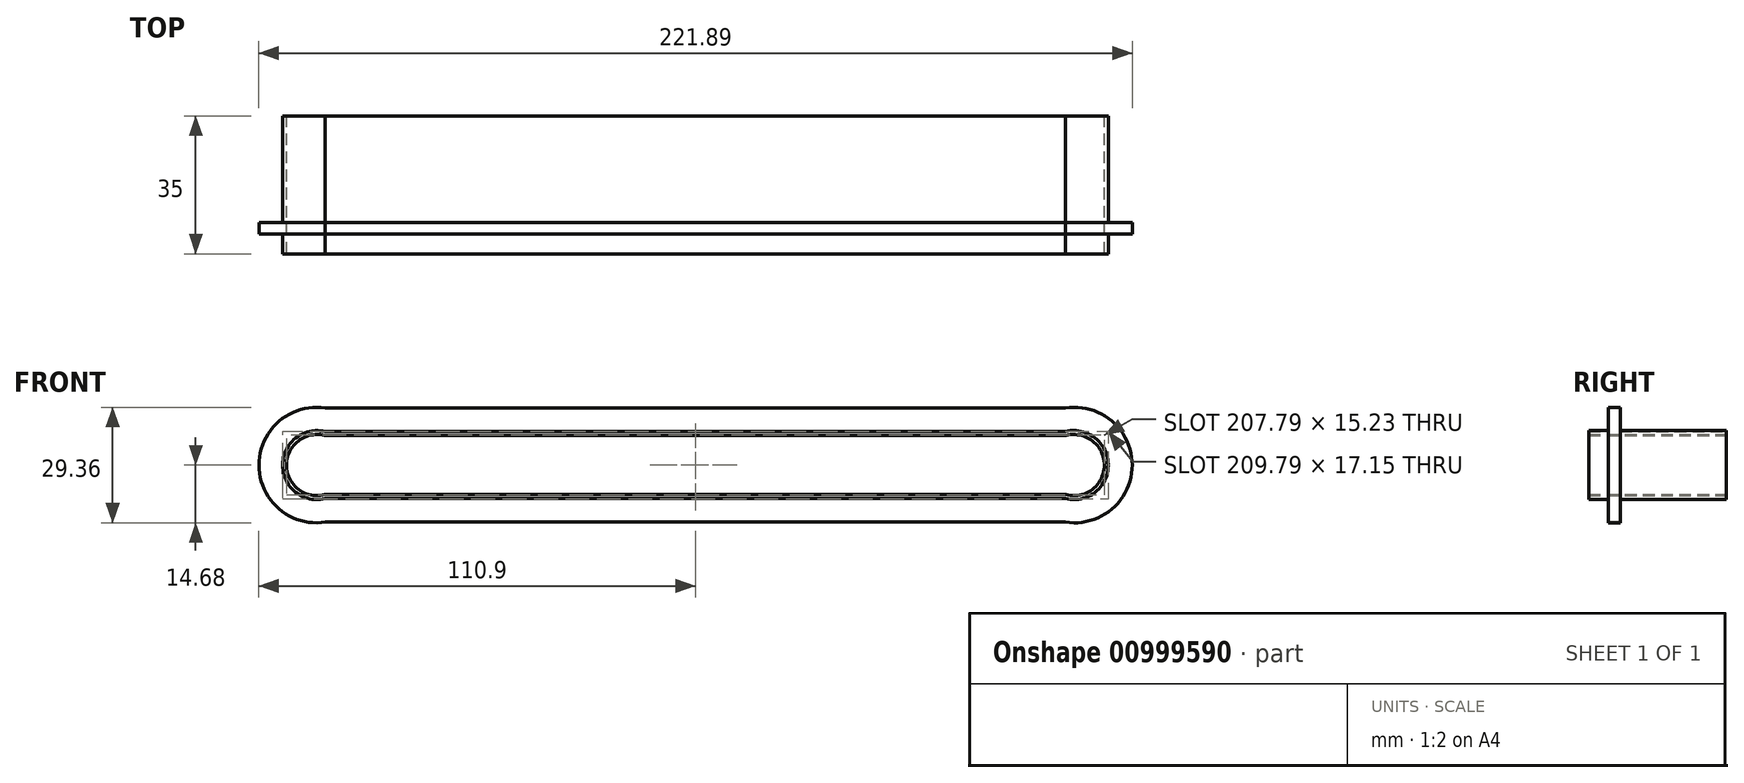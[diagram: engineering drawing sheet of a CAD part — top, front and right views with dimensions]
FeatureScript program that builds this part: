
annotation { "Feature Type Name" : "Feature", "Feature Type Description" : "" }
export const myFeature = defineFeature(function(context is Context, id is Id, definition is map)
    precondition{}
    {
        {
            var Q0;
            Q0=qCreatedBy(makeId("Front.planeOp"),FACE);
            var sketch = newSketch(context, id + "F0", { "sketchPlane" : qUnion([Q0])});
            skLineSegment(sketch, "E0.bottom", {"start": v(105, 8.5) * mm, "end": v(-105, 8.5) * mm});
            skLineSegment(sketch, "E0.top", {"start": v(105, -8.5) * mm, "end": v(-105, -8.5) * mm});
            skLineSegment(sketch, "E0.left", {"start": v(105, 8.5) * mm, "end": v(105, -8.5) * mm});
            skLineSegment(sketch, "E0.right", {"start": v(-105, 8.5) * mm, "end": v(-105, -8.5) * mm});
            skPoint(sketch, "E0.middle", {"position": v(0, 0) * mm});
            skLineSegment(sketch, "E1", {"start": v(0, -8.5) * mm, "end": v(94, -8.5) * mm});
            skLineSegment(sketch, "E2", {"start": v(94, -8.5) * mm, "end": v(-94, -8.5) * mm});
            skLineSegment(sketch, "E3", {"start": v(0, 8.5) * mm, "end": v(94, 8.5) * mm});
            skLineSegment(sketch, "E4", {"start": v(94, 8.5) * mm, "end": v(-94, 8.5) * mm});
            skArc(sketch, "E5", {"start": v(-94, 8.5) * mm, "mid": v(-104.89, 0) * mm, "end": v(-94, -8.5) * mm});
            skArc(sketch, "E6", {"start": v(94, -8.5) * mm, "mid": v(104.9, 0) * mm, "end": v(94, 8.5) * mm});
            skLineSegment(sketch, "E7", {"start": v(94, 8.5) * mm, "end": v(94, 14.5) * mm});
            skLineSegment(sketch, "E8", {"start": v(94, -8.5) * mm, "end": v(94, -14.5) * mm});
            skLineSegment(sketch, "E9", {"start": v(-94, 8.5) * mm, "end": v(-94, 14.5) * mm});
            skLineSegment(sketch, "E10", {"start": v(-94, -8.5) * mm, "end": v(-94, -14.5) * mm});
            skLineSegment(sketch, "E11", {"start": v(-94, -14.5) * mm, "end": v(94, -14.5) * mm});
            skLineSegment(sketch, "E12", {"start": v(94, 14.5) * mm, "end": v(-94, 14.5) * mm});
            skLineSegment(sketch, "E13", {"start": v(-104.89, 0) * mm, "end": v(-110.89, 0) * mm});
            skLineSegment(sketch, "E14", {"start": v(105, 0) * mm, "end": v(111, 0) * mm});
            skArc(sketch, "E15", {"start": v(-94, 14.5) * mm, "mid": v(-110.89, 0) * mm, "end": v(-94, -14.5) * mm});
            skArc(sketch, "E16", {"start": v(94, -14.5) * mm, "mid": v(111, 0) * mm, "end": v(94, 14.5) * mm});
            skSolve(sketch);
        }
        {
            var Q0;
            {var subQ0=sQuery(id+"F0.wireOp",EDGE,"E6");var subQ1=sQuery(id+"F0.wireOp",EDGE,"E0.bottom");var subQ3=makeQuery(id+"F0.imprint","INTERSECT",VERTEX,{"derivedFrom":[subQ1,subQ0]});Q0=makeQuery(id+"F0.imprint","IMPRINT",FACE,{"disambiguationData":[TD([[makeQuery(id+"F0.imprint","IMPRINT",EDGE,{"disambiguationData":[TD([[subQ3,-1.0]])],"derivedFrom":subQ1}),-1.0]])]});}
            var Q1;
            {var subQ0=sQuery(id+"F0.wireOp",EDGE,"E5");var subQ1=sQuery(id+"F0.wireOp",EDGE,"E0.bottom");var subQ2=makeQuery(id+"F0.imprint","INTERSECT",VERTEX,{"derivedFrom":[subQ1,subQ0]});Q1=makeQuery(id+"F0.imprint","IMPRINT",FACE,{"disambiguationData":[TD([[makeQuery(id+"F0.imprint","IMPRINT",EDGE,{"disambiguationData":[TD([[subQ2,1.0]])],"derivedFrom":subQ1}),-1.0]])]});}
            var Q2;
            {var subQ0=sQuery(id+"F0.wireOp",EDGE,"E6");var subQ1=sQuery(id+"F0.wireOp",EDGE,"E0.top");var subQ3=makeQuery(id+"F0.imprint","INTERSECT",VERTEX,{"derivedFrom":[subQ1,subQ0]});Q2=makeQuery(id+"F0.imprint","IMPRINT",FACE,{"disambiguationData":[TD([[makeQuery(id+"F0.imprint","IMPRINT",EDGE,{"disambiguationData":[TD([[subQ3,-1.0]])],"derivedFrom":subQ1}),1.0]])]});}
            var Q3;
            {var subQ0=sQuery(id+"F0.wireOp",EDGE,"E5");var subQ1=sQuery(id+"F0.wireOp",EDGE,"E0.top");var subQ2=makeQuery(id+"F0.imprint","INTERSECT",VERTEX,{"derivedFrom":[subQ1,subQ0]});Q3=makeQuery(id+"F0.imprint","IMPRINT",FACE,{"disambiguationData":[TD([[makeQuery(id+"F0.imprint","IMPRINT",EDGE,{"disambiguationData":[TD([[subQ2,1.0]])],"derivedFrom":subQ1}),1.0]])]});}
            var Q4;
            {var subQ9=sQuery(id+"F0.wireOp",EDGE,"E0.bottom");var subQ12=makeQuery(id+"F0.imprint","IMPRINT",VERTEX,{"derivedFrom":subQ9});Q4=makeQuery(id+"F0.imprint","IMPRINT",FACE,{"disambiguationData":[TD([[makeQuery(id+"F0.imprint","IMPRINT",EDGE,{"disambiguationData":[TD([[subQ12,1.0]])],"derivedFrom":subQ9}),1.0]])]});}
            extrude(context, id + "F1", {"entities" : qUnion([Q0, Q1, Q2, Q3, Q4]), "depth" : 5 * mm, "offsetDistance" : 25 * mm, "hasSecondDirection" : true, "secondDirectionOppositeDirection" : true, "secondDirectionDepth" : 30 * mm});
        }
        {
            var Q0;
            Q0=makeQuery(id+"F1.opExtrude","CAP_FACE",FACE,{"disambiguationData":[OSD([sQuery(id+"F0.wireOp",EDGE,"E0.bottom"),sQuery(id+"F0.wireOp",EDGE,"E0.top"),sQuery(id+"F0.wireOp",EDGE,"E5"),sQuery(id+"F0.wireOp",EDGE,"E6")])],"isStart":false});
            var Q1;
            Q1=makeQuery(id+"F1.opExtrude","CAP_FACE",FACE,{"disambiguationData":[OSD([sQuery(id+"F0.wireOp",EDGE,"E0.bottom"),sQuery(id+"F0.wireOp",EDGE,"E0.top"),sQuery(id+"F0.wireOp",EDGE,"E5"),sQuery(id+"F0.wireOp",EDGE,"E6")])],"isStart":true});
            shell(context, id + "F2", {"entities" : qUnion([Q0, Q1]), "thickness" : 1 * mm});
        }
        {
            var Q0;
            {var subQ0=sQuery(id+"F0.wireOp",EDGE,"E7");Q0=makeQuery(id+"F0.imprint","IMPRINT",FACE,{"disambiguationData":[TD([[makeQuery(id+"F0.imprint","IMPRINT",EDGE,{"derivedFrom":subQ0}),1.0]])]});}
            var Q1;
            {var subQ0=sQuery(id+"F0.wireOp",EDGE,"E7");Q1=makeQuery(id+"F0.imprint","IMPRINT",FACE,{"disambiguationData":[TD([[makeQuery(id+"F0.imprint","IMPRINT",EDGE,{"derivedFrom":subQ0}),-1.0]])]});}
            var Q2;
            {var subQ0=sQuery(id+"F0.wireOp",EDGE,"E8");Q2=makeQuery(id+"F0.imprint","IMPRINT",FACE,{"disambiguationData":[TD([[makeQuery(id+"F0.imprint","IMPRINT",EDGE,{"derivedFrom":subQ0}),-1.0]])]});}
            var Q3;
            {var subQ0=sQuery(id+"F0.wireOp",EDGE,"E8");Q3=makeQuery(id+"F0.imprint","IMPRINT",FACE,{"disambiguationData":[TD([[makeQuery(id+"F0.imprint","IMPRINT",EDGE,{"derivedFrom":subQ0}),1.0]])]});}
            var Q4;
            {var subQ0=sQuery(id+"F0.wireOp",EDGE,"E0.left");var subQ1=sQuery(id+"F0.wireOp",EDGE,"E0.bottom");var subQ2=makeQuery(id+"F0.imprint","INTERSECT",VERTEX,{"derivedFrom":[subQ1,subQ0]});Q4=makeQuery(id+"F0.imprint","IMPRINT",FACE,{"disambiguationData":[TD([[makeQuery(id+"F0.imprint","IMPRINT",EDGE,{"disambiguationData":[TD([[subQ2,-1.0]])],"derivedFrom":subQ1}),1.0]])]});}
            var Q5;
            {var subQ0=sQuery(id+"F0.wireOp",EDGE,"E9");Q5=makeQuery(id+"F0.imprint","IMPRINT",FACE,{"disambiguationData":[TD([[makeQuery(id+"F0.imprint","IMPRINT",EDGE,{"derivedFrom":subQ0}),1.0]])]});}
            var Q6;
            {var subQ0=sQuery(id+"F0.wireOp",EDGE,"E5");var subQ1=sQuery(id+"F0.wireOp",EDGE,"E0.bottom");var subQ2=makeQuery(id+"F0.imprint","INTERSECT",VERTEX,{"derivedFrom":[subQ1,subQ0]});Q6=makeQuery(id+"F0.imprint","IMPRINT",FACE,{"disambiguationData":[TD([[makeQuery(id+"F0.imprint","IMPRINT",EDGE,{"disambiguationData":[TD([[subQ2,-1.0]])],"derivedFrom":subQ1}),1.0]])]});}
            var Q7;
            {var subQ0=sQuery(id+"F0.wireOp",EDGE,"E10");Q7=makeQuery(id+"F0.imprint","IMPRINT",FACE,{"disambiguationData":[TD([[makeQuery(id+"F0.imprint","IMPRINT",EDGE,{"derivedFrom":subQ0}),-1.0]])]});}
            var Q8;
            {var subQ0=sQuery(id+"F0.wireOp",EDGE,"E5");var subQ1=sQuery(id+"F0.wireOp",EDGE,"E0.top");var subQ2=makeQuery(id+"F0.imprint","INTERSECT",VERTEX,{"derivedFrom":[subQ1,subQ0]});Q8=makeQuery(id+"F0.imprint","IMPRINT",FACE,{"disambiguationData":[TD([[makeQuery(id+"F0.imprint","IMPRINT",EDGE,{"disambiguationData":[TD([[subQ2,-1.0]])],"derivedFrom":subQ1}),-1.0]])]});}
            extrude(context, id + "F3", {"entities" : qUnion([Q0, Q1, Q2, Q3, Q4, Q5, Q6, Q7, Q8]), "operationType" : NewBodyOperationType.ADD, "oppositeDirection" : true, "depth" : 3 * mm, "offsetDistance" : 25 * mm});
        }
    });
